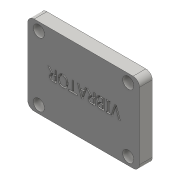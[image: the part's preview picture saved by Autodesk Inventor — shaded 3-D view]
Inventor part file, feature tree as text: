
AUTODESK INVENTOR PART (.ipt)
format: ipt  version: 2016 (Build 200138000, 138)  size: 271,360 bytes
history: native  units: mm
features: fillet x4, extrude x3, sketch x3
ambient origin geometry x8: Origin, YZ Plane, XZ Plane, XY Plane, X Axis, Y Axis, Z Axis, Center Point
bodies: Volumenkörper1 (feature_tree)
feature tree (10):
  extrude  "Extrusion1"  Depth=25.0mm
  fillet  "Rundung1"  Radius=4.0mm
  fillet  "Rundung2"  Radius=2.0mm
  fillet  "Rundung3"  Radius=2.0mm
  fillet  "Rundung4"  Radius=2.0mm
  extrude  "Extrusion11"  Depth=3.5mm
  extrude  "Extrusion13"  Depth=3.5mm
  sketch  "Skizze1"  dims[d0=35.0mm d1=25.0mm d2=4.0mm d3=0.0mm d20=2.0mm d21=2.0mm d22=2.0mm]
  sketch  "Skizze11"  dims[d23=2.0mm d36=3.5mm]
  sketch  "Skizze13"  dims[d37=3.5mm d38=3.5mm d39=3.5mm d40=10.0mm d41=0.0mm d44=1.0mm d45=0.0mm]
